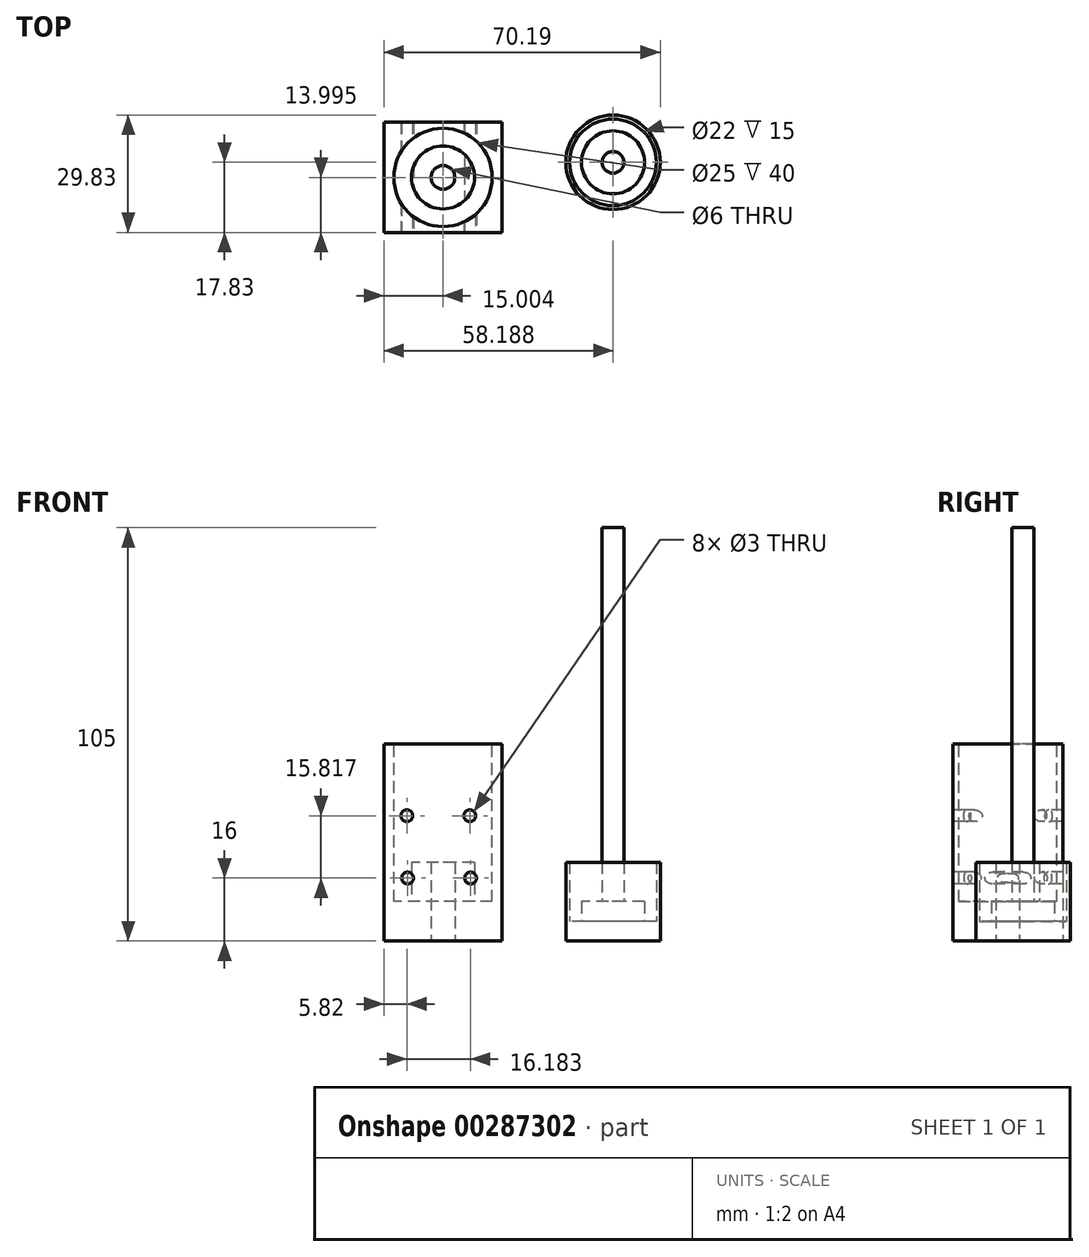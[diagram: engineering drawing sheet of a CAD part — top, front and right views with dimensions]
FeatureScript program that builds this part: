
annotation { "Feature Type Name" : "Feature", "Feature Type Description" : "" }
export const myFeature = defineFeature(function(context is Context, id is Id, definition is map)
    precondition{}
    {
        {
            var Q0;
            Q0=qCreatedBy(makeId("Top.planeOp"),FACE);
            var sketch = newSketch(context, id + "F0", { "sketchPlane" : qUnion([Q0])});
            skLineSegment(sketch, "E0.bottom", {"start": v(-34.02, 10.17) * mm, "end": v(-4.02, 10.17) * mm});
            skLineSegment(sketch, "E0.top", {"start": v(-34.02, -17.83) * mm, "end": v(-4.02, -17.83) * mm});
            skLineSegment(sketch, "E0.left", {"start": v(-34.02, 10.17) * mm, "end": v(-34.02, -17.83) * mm});
            skLineSegment(sketch, "E0.right", {"start": v(-4.02, 10.17) * mm, "end": v(-4.02, -17.83) * mm});
            skSolve(sketch);
        }
        {
            var Q0;
            Q0=makeQuery(id+"F0.imprint","IMPRINT",FACE,{"disambiguationData":[TD([[makeQuery(id+"F0.imprint","IMPRINT",EDGE,{"derivedFrom":sQuery(id+"F0.wireOp",EDGE,"E0.bottom")}),-1.0]])]});
            extrude(context, id + "F1", {"entities" : qUnion([Q0]), "depth" : 50 * mm});
        }
        {
            var Q0;
            Q0=makeQuery(id+"F1.opExtrude","CAP_FACE",FACE,{"disambiguationData":[OSD([sQuery(id+"F0.wireOp",EDGE,"E0.bottom"),sQuery(id+"F0.wireOp",EDGE,"E0.top"),sQuery(id+"F0.wireOp",EDGE,"E0.left"),sQuery(id+"F0.wireOp",EDGE,"E0.right")])],"isStart":false});
            var sketch = newSketch(context, id + "F2", { "sketchPlane" : qUnion([Q0])});
            skCircle(sketch, "E1", {"center": v(-19.02, -3.83) * mm, "radius": 12.5 * mm});
            skSolve(sketch);
        }
        {
            var Q0;
            Q0=makeQuery(id+"F2.imprint","IMPRINT",FACE,{"disambiguationData":[TD([[makeQuery(id+"F2.imprint","IMPRINT",EDGE,{"derivedFrom":sQuery(id+"F2.wireOp",EDGE,"E1")}),1.0]])]});
            extrude(context, id + "F3", {"entities" : qUnion([Q0]), "operationType" : NewBodyOperationType.REMOVE, "oppositeDirection" : true, "depth" : 40 * mm});
        }
        {
            var Q0;
            Q0=makeQuery(id+"F3.boolean.opBoolean","COPY",FACE,{"derivedFrom":makeQuery(id+"F3.opExtrude","CAP_FACE",FACE,{"disambiguationData":[OSD([sQuery(id+"F2.wireOp",EDGE,"E1")])],"isStart":false})});
            var sketch = newSketch(context, id + "F4", { "sketchPlane" : qUnion([Q0])});
            skCircle(sketch, "E2", {"center": v(-19.02, -3.83) * mm, "radius": 8 * mm});
            skCircle(sketch, "E3", {"center": v(-19.02, -3.83) * mm, "radius": 3 * mm});
            skSolve(sketch);
        }
        {
            var Q0;
            Q0=makeQuery(id+"F4.imprint","IMPRINT",FACE,{"disambiguationData":[TD([[makeQuery(id+"F4.imprint","IMPRINT",EDGE,{"derivedFrom":sQuery(id+"F4.wireOp",EDGE,"E2")}),1.0]])]});
            extrude(context, id + "F5", {"entities" : qUnion([Q0]), "operationType" : NewBodyOperationType.ADD, "depth" : 10 * mm});
        }
        {
            var Q0;
            Q0=qCreatedBy(makeId("Top.planeOp"),FACE);
            var sketch = newSketch(context, id + "F6", { "sketchPlane" : qUnion([Q0])});
            skCircle(sketch, "E4", {"center": v(24.17, 0) * mm, "radius": 12 * mm});
            skCircle(sketch, "E5", {"center": v(24.17, 0) * mm, "radius": 8 * mm});
            skCircle(sketch, "E6", {"center": v(24.17, 0) * mm, "radius": 11 * mm});
            skCircle(sketch, "E7", {"center": v(24.17, 0) * mm, "radius": 2.75 * mm});
            skSolve(sketch);
        }
        {
            var Q0;
            Q0=makeQuery(id+"F6.imprint","IMPRINT",FACE,{"disambiguationData":[TD([[makeQuery(id+"F6.imprint","IMPRINT",EDGE,{"derivedFrom":sQuery(id+"F6.wireOp",EDGE,"E5")}),1.0]])]});
            extrude(context, id + "F7", {"entities" : qUnion([Q0]), "depth" : 10 * mm});
        }
        {
            var Q0;
            Q0=makeQuery(id+"F6.imprint","IMPRINT",FACE,{"disambiguationData":[TD([[makeQuery(id+"F6.imprint","IMPRINT",EDGE,{"derivedFrom":sQuery(id+"F6.wireOp",EDGE,"E4")}),1.0]])]});
            extrude(context, id + "F8", {"entities" : qUnion([Q0]), "depth" : 20 * mm});
        }
        {
            var Q0;
            Q0=makeQuery(id+"F6.imprint","IMPRINT",FACE,{"disambiguationData":[TD([[makeQuery(id+"F6.imprint","IMPRINT",EDGE,{"derivedFrom":sQuery(id+"F6.wireOp",EDGE,"E5")}),1.0]])]});
            var Q1;
            Q1=makeQuery(id+"F6.imprint","IMPRINT",FACE,{"disambiguationData":[TD([[makeQuery(id+"F6.imprint","IMPRINT",EDGE,{"derivedFrom":sQuery(id+"F6.wireOp",EDGE,"E5")}),-1.0]])]});
            var Q2;
            Q2=makeQuery(id+"F6.imprint","IMPRINT",FACE,{"disambiguationData":[TD([[makeQuery(id+"F6.imprint","IMPRINT",EDGE,{"derivedFrom":sQuery(id+"F6.wireOp",EDGE,"E4")}),1.0]])]});
            var Q3;
            Q3=makeQuery(id+"F6.imprint","IMPRINT",FACE,{"disambiguationData":[TD([[makeQuery(id+"F6.imprint","IMPRINT",EDGE,{"derivedFrom":sQuery(id+"F6.wireOp",EDGE,"E7")}),1.0]])]});
            extrude(context, id + "F9", {"entities" : qUnion([Q0, Q1, Q2, Q3]), "operationType" : NewBodyOperationType.ADD, "depth" : 5 * mm});
        }
        {
            var Q0;
            Q0=makeQuery(id+"F5.boolean.opBoolean","SPLIT",FACE,{"disambiguationData":[TD([makeQuery(id+"F5.opExtrude","SWEPT_FACE",FACE,{"disambiguationData":[OSD([sQuery(id+"F4.wireOp",EDGE,"E3")])]})])],"derivedFrom":makeQuery(id+"F3.boolean.opBoolean","COPY",FACE,{"derivedFrom":makeQuery(id+"F3.opExtrude","CAP_FACE",FACE,{"disambiguationData":[OSD([sQuery(id+"F2.wireOp",EDGE,"E1")])],"isStart":false})})});
            extrude(context, id + "F10", {"entities" : qUnion([Q0]), "operationType" : NewBodyOperationType.REMOVE, "endBound" : BoundingType.THROUGH_ALL, "oppositeDirection" : true, "depth" : 25 * mm});
        }
        {
            var Q0;
            Q0=makeQuery(id+"F9.boolean.opBoolean","SPLIT",FACE,{"disambiguationData":[TD([makeQuery(id+"F7.opExtrude","SWEPT_FACE",FACE,{"disambiguationData":[OSD([sQuery(id+"F6.wireOp",EDGE,"E7")])]})])],"derivedFrom":makeQuery(id+"F9.opExtrude","CAP_FACE",FACE,{"disambiguationData":[OSD([sQuery(id+"F6.wireOp",EDGE,"E4")])],"isStart":false})});
            extrude(context, id + "F11", {"entities" : qUnion([Q0]), "operationType" : NewBodyOperationType.ADD, "depth" : 100 * mm});
        }
        {
            var Q0;
            Q0=makeQuery(id+"F1.opExtrude","SWEPT_FACE",FACE,{"disambiguationData":[OSD([sQuery(id+"F0.wireOp",EDGE,"E0.top")])]});
            var sketch = newSketch(context, id + "F12", { "sketchPlane" : qUnion([Q0])});
            skCircle(sketch, "E8", {"center": v(-20.02, 8) * mm, "radius": 1.5 * mm});
            skCircle(sketch, "E9.0.1.0", {"center": v(-20.02, 24) * mm, "radius": 1.5 * mm});
            skCircle(sketch, "E9.0.2.0", {"center": v(-20.02, 40) * mm, "radius": 1.5 * mm});
            skLineSegment(sketch, "E9.direction1", {"start": v(-20.02, 8) * mm, "end": v(4.98, 8) * mm, "construction": true});
            skLineSegment(sketch, "E9.direction2", {"start": v(-20.02, 8) * mm, "end": v(-20.02, 24) * mm, "construction": true});
            skCircle(sketch, "E10.1.0", {"center": v(-14.36, 21.66) * mm, "radius": 1.5 * mm});
            skCircle(sketch, "E10.1.1", {"center": v(-25.67, 10.34) * mm, "radius": 1.5 * mm});
            skCircle(sketch, "E10.2.0", {"center": v(-12.02, 16) * mm, "radius": 1.5 * mm});
            skCircle(sketch, "E10.2.1", {"center": v(-28.02, 16) * mm, "radius": 1.5 * mm});
            skCircle(sketch, "E10.3.0", {"center": v(-14.36, 10.34) * mm, "radius": 1.5 * mm});
            skCircle(sketch, "E10.3.1", {"center": v(-25.67, 21.66) * mm, "radius": 1.5 * mm});
            skPoint(sketch, "E10.center", {"position": v(-20.02, 16) * mm});
            skLineSegment(sketch, "E10.anchor1", {"start": v(-20.02, 16) * mm, "end": v(-20.02, 24) * mm, "construction": true});
            skLineSegment(sketch, "E10.anchor2", {"start": v(-20.02, 16) * mm, "end": v(-14.36, 10.34) * mm, "construction": true});
            skCircle(sketch, "E11.1.0", {"center": v(-14.41, 37.53) * mm, "radius": 1.5 * mm});
            skCircle(sketch, "E11.1.1", {"center": v(-25.73, 26.21) * mm, "radius": 1.5 * mm});
            skCircle(sketch, "E11.2.0", {"center": v(-12.2, 31.82) * mm, "radius": 1.5 * mm});
            skCircle(sketch, "E11.2.1", {"center": v(-28.2, 31.82) * mm, "radius": 1.5 * mm});
            skCircle(sketch, "E11.3.0", {"center": v(-14.67, 26.21) * mm, "radius": 1.5 * mm});
            skCircle(sketch, "E11.3.1", {"center": v(-25.99, 37.53) * mm, "radius": 1.5 * mm});
            skPoint(sketch, "E11.center", {"position": v(-20.2, 32) * mm});
            skLineSegment(sketch, "E11.anchor1", {"start": v(-20.2, 32) * mm, "end": v(-20.02, 40) * mm, "construction": true});
            skLineSegment(sketch, "E11.anchor2", {"start": v(-20.2, 32) * mm, "end": v(-14.67, 26.21) * mm, "construction": true});
            skSolve(sketch);
        }
        {
            var Q0;
            Q0=makeQuery(id+"F12.imprint","IMPRINT",FACE,{"disambiguationData":[TD([[makeQuery(id+"F12.imprint","IMPRINT",EDGE,{"derivedFrom":sQuery(id+"F12.wireOp",EDGE,"E11.2.1")}),1.0]])]});
            var Q1;
            Q1=makeQuery(id+"F12.imprint","IMPRINT",FACE,{"disambiguationData":[TD([[makeQuery(id+"F12.imprint","IMPRINT",EDGE,{"derivedFrom":sQuery(id+"F12.wireOp",EDGE,"E11.2.0")}),1.0]])]});
            var Q2;
            Q2=makeQuery(id+"F12.imprint","IMPRINT",FACE,{"disambiguationData":[TD([[makeQuery(id+"F12.imprint","IMPRINT",EDGE,{"derivedFrom":sQuery(id+"F12.wireOp",EDGE,"E10.2.0")}),1.0]])]});
            var Q3;
            Q3=makeQuery(id+"F12.imprint","IMPRINT",FACE,{"disambiguationData":[TD([[makeQuery(id+"F12.imprint","IMPRINT",EDGE,{"derivedFrom":sQuery(id+"F12.wireOp",EDGE,"E10.2.1")}),1.0]])]});
            extrude(context, id + "F13", {"entities" : qUnion([Q0, Q1, Q2, Q3]), "operationType" : NewBodyOperationType.REMOVE, "endBound" : BoundingType.THROUGH_ALL, "oppositeDirection" : true, "depth" : 25 * mm});
        }
    });
